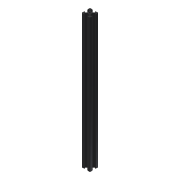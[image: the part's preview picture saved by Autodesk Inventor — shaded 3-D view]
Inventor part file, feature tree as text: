
AUTODESK INVENTOR PART (.ipt)
format: ipt  version: 2014 (Build 180170000, 170)  size: 374,272 bytes
history: native  units: mm
features: other x20, fillet x3, extrude x2, sketch x2, pattern_circular x1
ambient origin geometry x8: Origin, YZ Plane, XZ Plane, XY Plane, X Axis, Y Axis, Z Axis, Center Point
bodies: Solid1 (feature_tree)
feature tree (28):
  other  "Table"
  other  "Length = 50 mm"
  other  "Length = 75"
  other  "Length = 100"
  other  "Length = 150 mm"
  other  "Length = 125 mm"
  other  "Length = 175 mm"
  other  "Length = 200 mm"
  other  "Length = 250 mm"
  other  "Length = 225 mm"
  other  "Length = 300 mm"
  other  "Length = 325 mm"
  other  "Length = 350 mm"
  other  "Length = 400 mm"
  other  "Length = 375 mm"
  other  "Length = 450 mm"
  other  "Length = 425 mm"
  other  "Length = 475 mm"
  other  "Length = 500 mm"
  other  "Length = 275 mm"
  extrude  "Extrusion1"  Depth=8.76mm
  extrude  "Extrusion2"  Depth=0.75mm
  pattern_circular  "Circular Pattern1"  [2 undecoded]
  fillet  "Fillet9"  Radius=8.1mm
  fillet  "Fillet10"  Radius=2.14mm
  fillet  "Fillet11"  Radius=200.0mm
  sketch  "Sketch1"  dims[d0=8.76mm d1=5.0mm]
  sketch  "Sketch2"  dims[d3=0.0mm d4=12.5mm d5=2.14mm d6=8.1mm d7=2.14mm d8=200.0mm d9=0.0mm d10=40.0mm d11=360.0deg d23=1.0mm d24=0.75mm d25=0.75mm]
note: 2 required parameter values undecoded (feature->parameter linkage not recoverable at this tier; creation-order binding heuristic only, values carry confidence <= 0.55)
